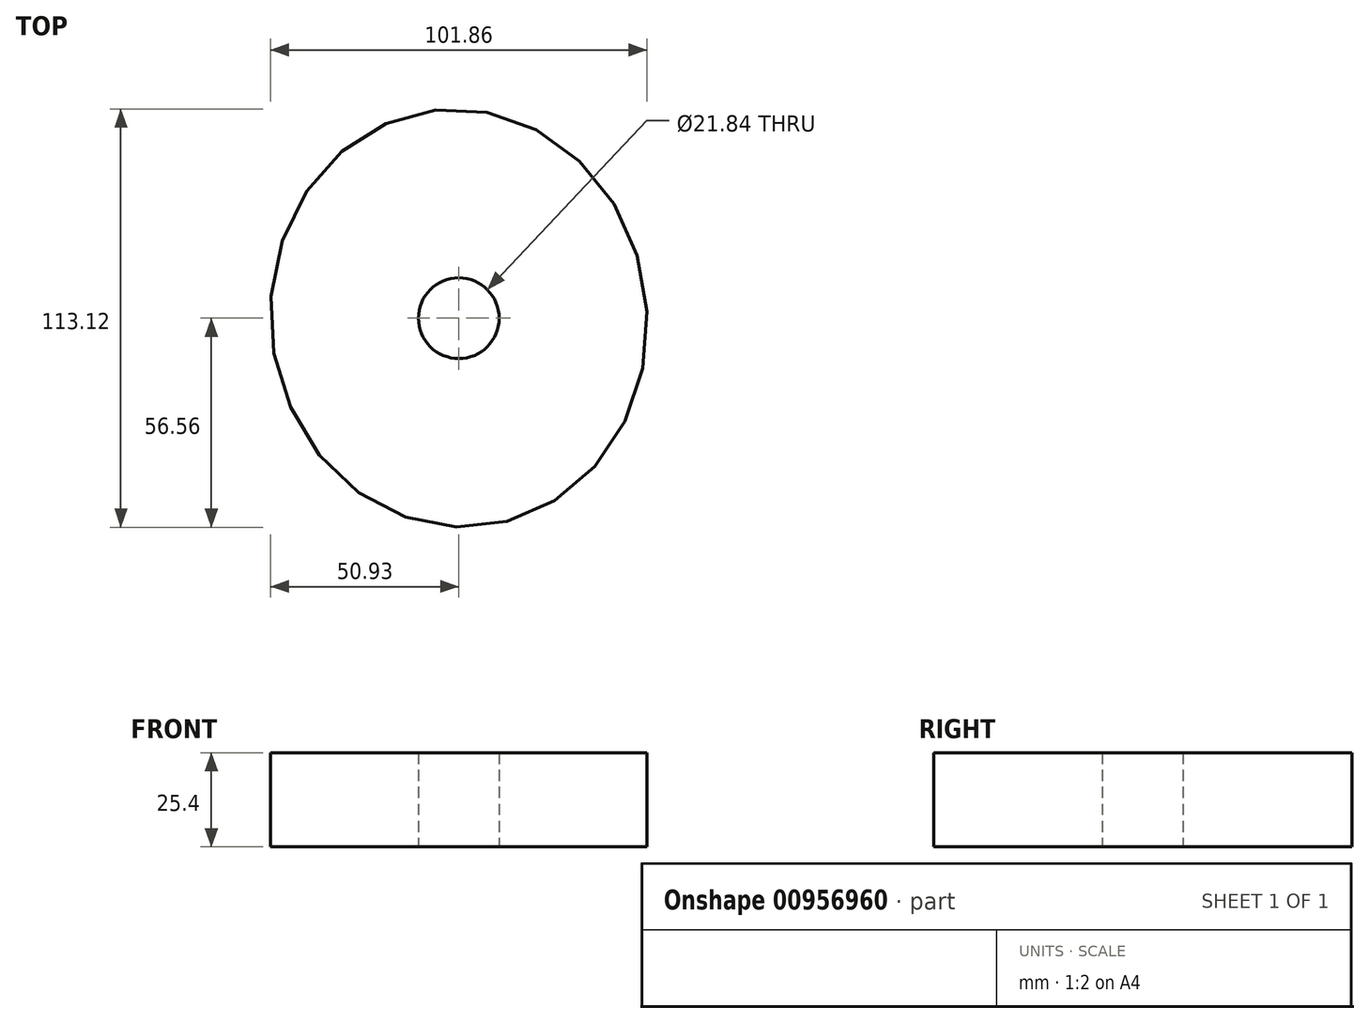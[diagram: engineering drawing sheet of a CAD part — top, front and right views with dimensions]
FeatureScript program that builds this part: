
annotation { "Feature Type Name" : "Feature", "Feature Type Description" : "" }
export const myFeature = defineFeature(function(context is Context, id is Id, definition is map)
    precondition{}
    {
        {
            var Q0;
            Q0=qCreatedBy(makeId("Top.planeOp"),FACE);
            var sketch = newSketch(context, id + "F0", { "sketchPlane" : qUnion([Q0])});
            skCircle(sketch, "E0", {"center": v(0, 0) * mm, "radius": 10.92 * mm});
            skCircle(sketch, "E1", {"center": v(0, 0) * mm, "radius": 34.07 * mm});
            skCircle(sketch, "E2", {"center": v(0, 0) * mm, "radius": 30.42 * mm});
            skCircle(sketch, "E3", {"center": v(0, 0) * mm, "radius": 26.2 * mm});
            skCircle(sketch, "E4", {"center": v(0, 0) * mm, "radius": 22.09 * mm});
            skEllipse(sketch, "E5", {"center": v(0, 0) * mm, "majorRadius": 56.63 * mm, "minorRadius": 50.85 * mm, "majorAxis": v(-0.11, 1)});
            skCircle(sketch, "E6", {"center": v(0, 0) * mm, "radius": 40.71 * mm});
            skSolve(sketch);
        }
        {
            var Q0;
            Q0 = qSketchRegion(id + "F0", true);
            var Q1;
            Q1=makeQuery(id+"F0.imprint","IMPRINT",FACE,{"disambiguationData":[TD([[makeQuery(id+"F0.imprint","IMPRINT",EDGE,{"derivedFrom":sQuery(id+"F0.wireOp",EDGE,"E1")}),-1.0]])]});
            var Q2;
            Q2=makeQuery(id+"F0.imprint","IMPRINT",FACE,{"disambiguationData":[TD([[makeQuery(id+"F0.imprint","IMPRINT",EDGE,{"derivedFrom":sQuery(id+"F0.wireOp",EDGE,"E1")}),1.0]])]});
            var Q3;
            Q3=makeQuery(id+"F0.imprint","IMPRINT",FACE,{"disambiguationData":[TD([[makeQuery(id+"F0.imprint","IMPRINT",EDGE,{"derivedFrom":sQuery(id+"F0.wireOp",EDGE,"E2")}),1.0]])]});
            var Q4;
            Q4=makeQuery(id+"F0.imprint","IMPRINT",FACE,{"disambiguationData":[TD([[makeQuery(id+"F0.imprint","IMPRINT",EDGE,{"derivedFrom":sQuery(id+"F0.wireOp",EDGE,"E3")}),1.0]])]});
            var Q5;
            Q5=makeQuery(id+"F0.imprint","IMPRINT",FACE,{"disambiguationData":[TD([[makeQuery(id+"F0.imprint","IMPRINT",EDGE,{"derivedFrom":sQuery(id+"F0.wireOp",EDGE,"E0")}),-1.0]])]});
            extrude(context, id + "F1", {"entities" : qUnion([Q0, Q1, Q2, Q3, Q4, Q5]), "depth" : 25.4 * mm, "offsetDistance" : 25.4 * mm});
        }
    });
